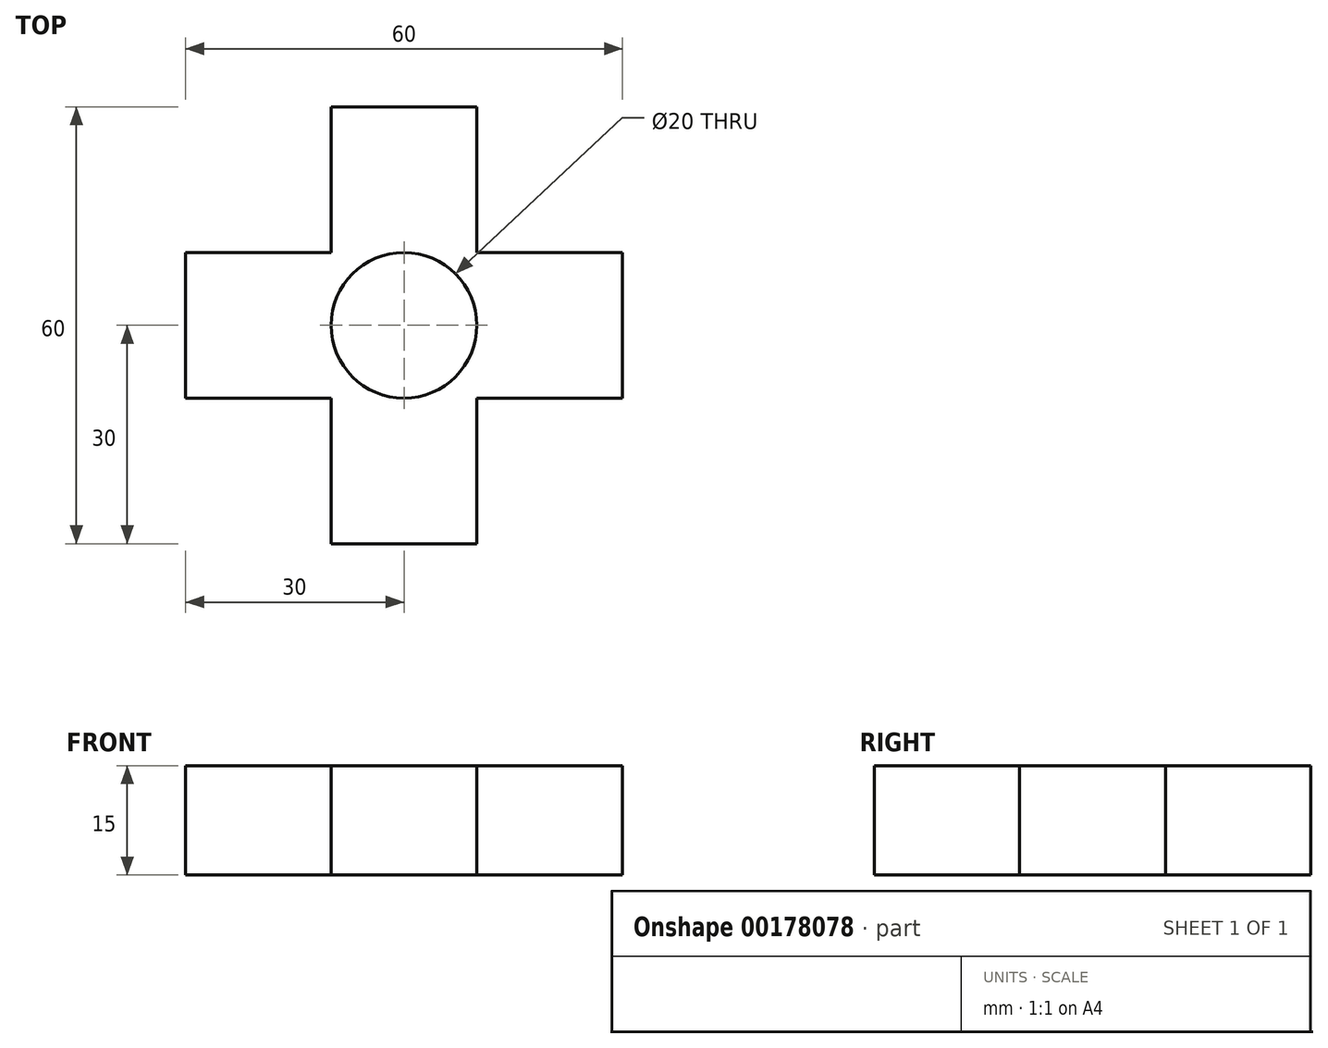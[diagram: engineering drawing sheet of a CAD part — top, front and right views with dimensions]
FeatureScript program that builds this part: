
annotation { "Feature Type Name" : "Feature", "Feature Type Description" : "" }
export const myFeature = defineFeature(function(context is Context, id is Id, definition is map)
    precondition{}
    {
        {
            var Q0;
            Q0=qCreatedBy(makeId("Top.planeOp"),FACE);
            var sketch = newSketch(context, id + "F0", { "sketchPlane" : qUnion([Q0])});
            skLineSegment(sketch, "E0", {"start": v(0, 0) * mm, "end": v(30, 0) * mm});
            skLineSegment(sketch, "E1", {"start": v(30, 0) * mm, "end": v(30, 10) * mm});
            skLineSegment(sketch, "E2", {"start": v(30, 10) * mm, "end": v(10, 10) * mm});
            skLineSegment(sketch, "E3", {"start": v(10, 10) * mm, "end": v(10, 30) * mm});
            skLineSegment(sketch, "E4", {"start": v(10, 30) * mm, "end": v(0, 30) * mm});
            skLineSegment(sketch, "E5.MirrorCS", {"start": v(-10, 30) * mm, "end": v(0, 30) * mm});
            skLineSegment(sketch, "E6.MirrorCS", {"start": v(-10, 10) * mm, "end": v(-10, 30) * mm});
            skLineSegment(sketch, "E7.MirrorCS", {"start": v(-30, 10) * mm, "end": v(-10, 10) * mm});
            skLineSegment(sketch, "E8.MirrorCS", {"start": v(-30, 0) * mm, "end": v(-30, 10) * mm});
            skLineSegment(sketch, "E9.MirrorCS", {"start": v(0, 0) * mm, "end": v(-30, 0) * mm});
            skLineSegment(sketch, "E10.MirrorCS", {"start": v(-30, 0) * mm, "end": v(-30, -10) * mm});
            skLineSegment(sketch, "E11.MirrorCS", {"start": v(-30, -10) * mm, "end": v(-10, -10) * mm});
            skLineSegment(sketch, "E12.MirrorCS", {"start": v(-10, -10) * mm, "end": v(-10, -30) * mm});
            skLineSegment(sketch, "E13.MirrorCS", {"start": v(-10, -30) * mm, "end": v(0, -30) * mm});
            skLineSegment(sketch, "E14.MirrorCS", {"start": v(10, -30) * mm, "end": v(0, -30) * mm});
            skLineSegment(sketch, "E15.MirrorCS", {"start": v(10, -10) * mm, "end": v(10, -30) * mm});
            skLineSegment(sketch, "E16.MirrorCS", {"start": v(30, -10) * mm, "end": v(10, -10) * mm});
            skLineSegment(sketch, "E17.MirrorCS", {"start": v(30, 0) * mm, "end": v(30, -10) * mm});
            skCircle(sketch, "E18", {"center": v(0, 0) * mm, "radius": 10 * mm});
            skSolve(sketch);
        }
        {
            var Q0;
            Q0 = qSketchRegion(id + "F0", true);
            extrude(context, id + "F1", {"entities" : qUnion([Q0]), "depth" : 15 * mm});
        }
    });
